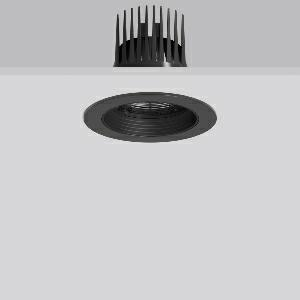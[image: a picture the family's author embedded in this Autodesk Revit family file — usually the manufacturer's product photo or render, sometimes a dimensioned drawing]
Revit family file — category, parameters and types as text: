
# Revit family: heledon_maxi_e_901762_003_1_f223
name_source: partatom
category: Lighting Fixtures
units: mm (PartAtom-declared; Revit-internal decimal feet)

## family parameters
Cut with Voids When Loaded = No
Host = Face
Light Source = No
Part Type = Normal
Room Calculation Point = No
Round Connector Dimension = Use Diameter
Shared = No

## types (1)
- HELEDON maxi E (1 x LED Modul 940, 2950 lm, 4000)
    Apparent Load = 25 VA
    Approval mark = CE
    CIE Flux Codes = 96 100 100 100 100
    Color Rendering = 92
    Color Temperature = 4000
    Default Elevation = 1800 mm
    Description = Series: HELEDON maxi
Round recessed downlight. Housing: die-cast aluminium, powder-coated. Black plastic ring and recessed LED to prevent glare from the side. Optical assembly with lens made of plastic (polycarbonate) for the best homogeneous light distribution - can be changed without tools. Best colour rendering index Ra>90. Suitable for Recessed ceiling mounting. Installation without tools thanks to spring fastening system. Including separate LED converter with connecting cable 600 mm.High quality converter without flickering and stroboscopic effect. Through-wiring box (5 pole) available as accessory. The following accessories can be mounted without use of tools: interchangeable lenses, decorative glasses, honeycomb louvre, clear and frosted diffusers, white interchangeable plastic ring. 
Colour: deep black, matt (RAL 9005)
Diameter: 162 mm
Height: 3 mm
Cut-out diameter: 152 mm
Recess height: 200 mm
Luminaire: recess height: 135 mm
Lamp: LED
Socket: without socket
Colour temperature: 4000K
Colour rendering index (CRI): 92
System power: 25 W
Rated luminous flux: 2950 lm
Luminous efficiency: 118 lm/W
Control gear: Regulated power supply
Protection class: II
Type of protection: IP 20
    Height = 0 mm  [stored 0 ft]
    Lamp = 1 x LED Modul 940
    Lamp Light Flux = 2950 lm
    Lamp count = 1
    Length = 162 mm
    Lifetime = 50000 h
    Luminous efficacy = 118 lm/W
    Manufacturer = RZB
    ModVariant = No
    Model = 901762.003.1
    Mounting Place = Ceiling
    Mounting Type = Recessed
    Number of Poles = 1
    OnlyDefault = Yes
    Power Factor = 1
    Product Name = HELEDON maxi E
    Product group = Recessed downlights
    ProductGroupID = 402
    Protection Class = Protection class II
    Protection Degree = IP 20
    RLX_Detail_Level = 1
    RLX_Emergency_Light_Flux = 0 lm
    RLX_Emergency_Type = 0
    RLX_Emergency_Type_DB = No
    RlxData = <blob elided: 121573 chars, md5=a6614f86>
    Socket = socket
    Standby Power = 0 W
    System Light Flux = 2950 lm
    System Power = 25 W
    Type Comments = Product without accessories
    Type Image = 901663.003.jpg
    URL = http://relux.com
    VarID = ---
    Voltage = 230 V
    Voltage Range = 220-240 V
    Weight = 0.00 kg
    Width = 0 mm  [stored 0 ft]

note: [stored X ft] marks values corroborated as IEEE doubles in the binary element streams (Revit-internal decimal feet)

## geometry (parser evidence)
native form markers: Blend x4, Sweep x12
no freeform markers — native parametric forms only
